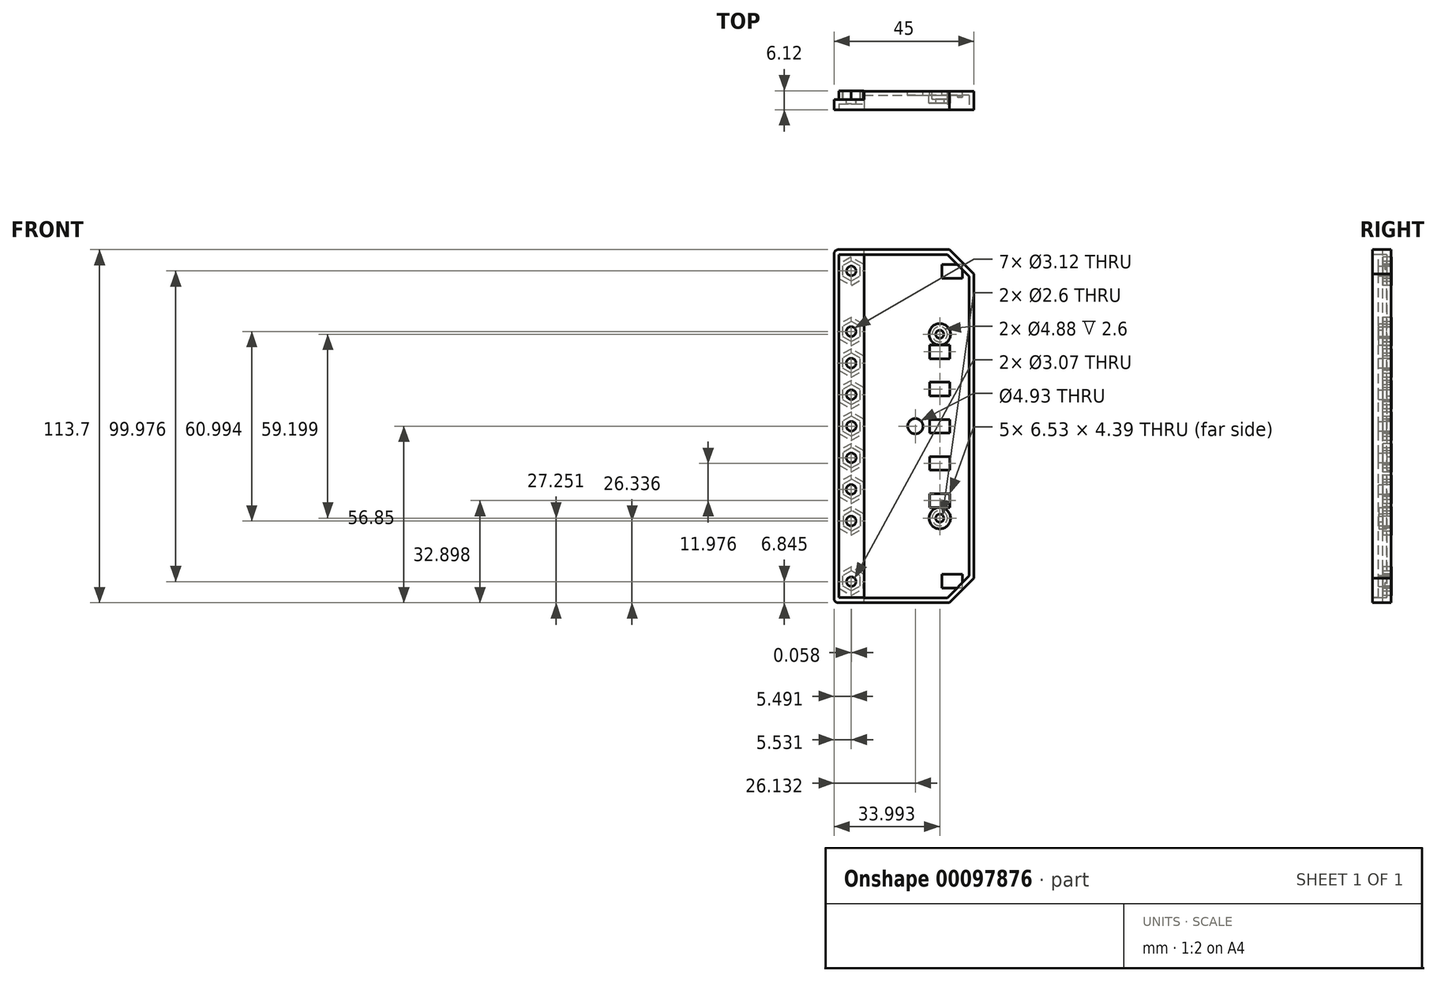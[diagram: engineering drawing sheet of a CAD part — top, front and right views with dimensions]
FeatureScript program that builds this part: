
annotation { "Feature Type Name" : "Feature", "Feature Type Description" : "" }
export const myFeature = defineFeature(function(context is Context, id is Id, definition is map)
    precondition{}
    {
        {
            var Q0;
            Q0=qCreatedBy(makeId("Top.planeOp"),FACE);
            var sketch = newSketch(context, id + "F0", { "sketchPlane" : qUnion([Q0])});
            skLineSegment(sketch, "E0.rect.bottom", {"start": v(22.5, -3) * mm, "end": v(-22.5, -3) * mm});
            skLineSegment(sketch, "E0.rect.top", {"start": v(22.5, 3) * mm, "end": v(-22.5, 3) * mm});
            skLineSegment(sketch, "E0.rect.left", {"start": v(22.5, -3) * mm, "end": v(22.5, 3) * mm});
            skLineSegment(sketch, "E0.rect.right", {"start": v(-22.5, -3) * mm, "end": v(-22.5, 3) * mm});
            skPoint(sketch, "E0.rect.middle", {"position": v(0, 0) * mm});
            skLineSegment(sketch, "E1", {"start": v(-12.85, 3) * mm, "end": v(-12.85, 0.3) * mm});
            skLineSegment(sketch, "E2", {"start": v(-12.85, 0.3) * mm, "end": v(-22.5, 0.3) * mm});
            skSolve(sketch);
        }
        {
            var Q0;
            Q0=qSketchRegion(id+"F0",true);
            extrude(context, id + "F1", {"entities" : qUnion([Q0]), "oppositeDirection" : true, "depth" : 113.7 * mm});
        }
        {
            var Q0;
            {var subQ1=sQuery(id+"F0.wireOp",EDGE,"E1");Q0=makeQuery(id+"F0.imprint","IMPRINT",FACE,{"disambiguationData":[TD([[makeQuery(id+"F0.imprint","IMPRINT",EDGE,{"derivedFrom":subQ1}),-1.0]])]});}
            extrude(context, id + "F2", {"entities" : qUnion([Q0]), "operationType" : NewBodyOperationType.REMOVE, "oppositeDirection" : true, "depth" : 113.93 * mm});
        }
        {
            var Q0;
            Q0=makeQuery(id+"F1.opExtrude","SWEPT_FACE",FACE,{"disambiguationData":[OSD([sQuery(id+"F0.wireOp",EDGE,"E0.rect.bottom")])]});
            var sketch = newSketch(context, id + "F3", { "sketchPlane" : qUnion([Q0])});
            skLineSegment(sketch, "E3.bottom", {"start": v(-22.5, -113.59) * mm, "end": v(-12.85, -113.59) * mm});
            skLineSegment(sketch, "E3.top", {"start": v(-22.5, 0) * mm, "end": v(-12.85, 0) * mm});
            skLineSegment(sketch, "E3.left", {"start": v(-22.5, -113.59) * mm, "end": v(-22.5, 0) * mm});
            skLineSegment(sketch, "E3.right", {"start": v(-12.85, -113.59) * mm, "end": v(-12.85, 0) * mm});
            skLineSegment(sketch, "E4.bottom", {"start": v(-20.92, -112) * mm, "end": v(-12.85, -112) * mm});
            skLineSegment(sketch, "E4.top", {"start": v(-20.92, -1.58) * mm, "end": v(-12.85, -1.58) * mm});
            skLineSegment(sketch, "E4.left", {"start": v(-20.92, -112) * mm, "end": v(-20.92, -1.58) * mm});
            skLineSegment(sketch, "E4.right", {"start": v(-12.85, -112) * mm, "end": v(-12.85, -1.58) * mm});
            skSolve(sketch);
        }
        {
            var Q0;
            Q0=makeQuery(id+"F3.imprint","IMPRINT",FACE,{"disambiguationData":[TD([[makeQuery(id+"F3.imprint","IMPRINT",EDGE,{"derivedFrom":sQuery(id+"F3.wireOp",EDGE,"E4.bottom")}),1.0]])]});
            extrude(context, id + "F4", {"entities" : qUnion([Q0]), "operationType" : NewBodyOperationType.REMOVE, "oppositeDirection" : true, "depth" : 1.9 * mm});
        }
        {
            var Q0;
            Q0=makeQuery(id+"F1.opExtrude","CAP_EDGE",EDGE,{"disambiguationData":[OSD([sQuery(id+"F0.wireOp",EDGE,"E0.rect.left")])],"isStart":false});
            chamfer(context, id + "F5", {"entities" : qUnion([Q0]), "width" : 7.87 * mm, "tangentPropagation" : true});
        }
        {
            var Q0;
            Q0=makeQuery(id+"F1.opExtrude","CAP_EDGE",EDGE,{"disambiguationData":[OSD([sQuery(id+"F0.wireOp",EDGE,"E0.rect.left")])],"isStart":true});
            chamfer(context, id + "F6", {"entities" : qUnion([Q0]), "width" : 7.87 * mm, "tangentPropagation" : true});
        }
        {
            var Q0;
            Q0=makeQuery(id+"F1.opExtrude","SWEPT_FACE",FACE,{"disambiguationData":[OSD([sQuery(id+"F0.wireOp",EDGE,"E0.rect.bottom")])]});
            var sketch = newSketch(context, id + "F7", { "sketchPlane" : qUnion([Q0])});
            skLineSegment(sketch, "E5.bottom", {"start": v(-12.85, -1.58) * mm, "end": v(21, -1.58) * mm});
            skLineSegment(sketch, "E5.top", {"start": v(-12.85, -112.15) * mm, "end": v(21, -112.15) * mm});
            skLineSegment(sketch, "E5.left", {"start": v(-12.85, -1.58) * mm, "end": v(-12.85, -112.15) * mm});
            skLineSegment(sketch, "E5.right", {"start": v(21, -1.58) * mm, "end": v(21, -112.15) * mm});
            skLineSegment(sketch, "E6", {"start": v(21, -105.06) * mm, "end": v(13.92, -112.15) * mm});
            skLineSegment(sketch, "E7", {"start": v(14, -1.58) * mm, "end": v(21, -8.58) * mm});
            skSolve(sketch);
        }
        {
            var Q0;
            {var subQ3=sQuery(id+"F7.wireOp",EDGE,"E5.left");Q0=makeQuery(id+"F7.imprint","IMPRINT",FACE,{"disambiguationData":[TD([[makeQuery(id+"F7.imprint","IMPRINT",EDGE,{"derivedFrom":subQ3}),-1.0]])]});}
            extrude(context, id + "F8", {"entities" : qUnion([Q0]), "operationType" : NewBodyOperationType.REMOVE, "oppositeDirection" : true, "depth" : 4.67 * mm});
        }
        {
            var Q0;
            Q0=makeQuery(id+"F1.opExtrude","SWEPT_FACE",FACE,{"disambiguationData":[OSD([sQuery(id+"F0.wireOp",EDGE,"E0.rect.top")])]});
            var sketch = newSketch(context, id + "F9", { "sketchPlane" : qUnion([Q0])});
            skLineSegment(sketch, "E8", {"start": v(12.85, -56.85) * mm, "end": v(-22.5, -56.85) * mm, "construction": true});
            skLineSegment(sketch, "E9.rect.bottom", {"start": v(-14.76, -59.05) * mm, "end": v(-8.23, -59.05) * mm});
            skLineSegment(sketch, "E9.rect.top", {"start": v(-14.76, -54.65) * mm, "end": v(-8.23, -54.65) * mm});
            skLineSegment(sketch, "E9.rect.left", {"start": v(-14.76, -59.05) * mm, "end": v(-14.76, -54.65) * mm});
            skLineSegment(sketch, "E9.rect.right", {"start": v(-8.23, -59.05) * mm, "end": v(-8.23, -54.65) * mm});
            skPoint(sketch, "E9.rect.middle", {"position": v(-11.5, -56.85) * mm});
            skCircle(sketch, "E10", {"center": v(-3.63, -56.85) * mm, "radius": 2.46 * mm});
            skLineSegment(sketch, "E11.0.1.0", {"start": v(-8.23, -47.07) * mm, "end": v(-8.23, -42.68) * mm});
            skLineSegment(sketch, "E11.0.1.1", {"start": v(-14.76, -47.07) * mm, "end": v(-8.23, -47.07) * mm});
            skLineSegment(sketch, "E11.0.1.2", {"start": v(-14.76, -47.07) * mm, "end": v(-14.76, -42.68) * mm});
            skLineSegment(sketch, "E11.0.1.3", {"start": v(-14.76, -42.68) * mm, "end": v(-8.23, -42.68) * mm});
            skLineSegment(sketch, "E11.0.2.0", {"start": v(-8.23, -35.1) * mm, "end": v(-8.23, -30.7) * mm});
            skLineSegment(sketch, "E11.0.2.1", {"start": v(-14.76, -35.1) * mm, "end": v(-8.23, -35.1) * mm});
            skLineSegment(sketch, "E11.0.2.2", {"start": v(-14.76, -35.1) * mm, "end": v(-14.76, -30.7) * mm});
            skLineSegment(sketch, "E11.0.2.3", {"start": v(-14.76, -30.7) * mm, "end": v(-8.23, -30.7) * mm});
            skLineSegment(sketch, "E11.direction1", {"start": v(-8.23, -59.05) * mm, "end": v(17.17, -59.05) * mm, "construction": true});
            skLineSegment(sketch, "E11.direction2", {"start": v(-8.23, -59.05) * mm, "end": v(-8.23, -47.07) * mm, "construction": true});
            skLineSegment(sketch, "E12.0.1.0", {"start": v(-8.23, -71.02) * mm, "end": v(-8.23, -66.63) * mm});
            skLineSegment(sketch, "E12.0.1.1", {"start": v(-14.76, -71.02) * mm, "end": v(-8.23, -71.02) * mm});
            skLineSegment(sketch, "E12.0.1.2", {"start": v(-14.76, -71.02) * mm, "end": v(-14.76, -66.63) * mm});
            skLineSegment(sketch, "E12.0.1.3", {"start": v(-14.76, -66.63) * mm, "end": v(-8.23, -66.63) * mm});
            skLineSegment(sketch, "E12.0.2.0", {"start": v(-8.23, -83) * mm, "end": v(-8.23, -78.6) * mm});
            skLineSegment(sketch, "E12.0.2.1", {"start": v(-14.76, -83) * mm, "end": v(-8.23, -83) * mm});
            skLineSegment(sketch, "E12.0.2.2", {"start": v(-14.76, -83) * mm, "end": v(-14.76, -78.6) * mm});
            skLineSegment(sketch, "E12.0.2.3", {"start": v(-14.76, -78.6) * mm, "end": v(-8.23, -78.6) * mm});
            skLineSegment(sketch, "E12.direction2", {"start": v(-8.23, -59.05) * mm, "end": v(-8.23, -71.02) * mm, "construction": true});
            skLineSegment(sketch, "E13.rect.bottom", {"start": v(-18.73, -9.2) * mm, "end": v(-12.2, -9.2) * mm});
            skLineSegment(sketch, "E13.rect.top", {"start": v(-18.73, -4.8) * mm, "end": v(-12.2, -4.8) * mm});
            skLineSegment(sketch, "E13.rect.left", {"start": v(-18.73, -9.2) * mm, "end": v(-18.73, -4.8) * mm});
            skLineSegment(sketch, "E13.rect.right", {"start": v(-12.2, -9.2) * mm, "end": v(-12.2, -4.8) * mm});
            skPoint(sketch, "E13.rect.middle", {"position": v(-15.47, -7) * mm});
            skLineSegment(sketch, "E14.rect.bottom", {"start": v(-18.73, -108.9) * mm, "end": v(-12.2, -108.9) * mm});
            skLineSegment(sketch, "E14.rect.top", {"start": v(-18.73, -104.5) * mm, "end": v(-12.2, -104.5) * mm});
            skLineSegment(sketch, "E14.rect.left", {"start": v(-18.73, -108.9) * mm, "end": v(-18.73, -104.5) * mm});
            skLineSegment(sketch, "E14.rect.right", {"start": v(-12.2, -108.9) * mm, "end": v(-12.2, -104.5) * mm});
            skPoint(sketch, "E14.rect.middle", {"position": v(-15.47, -106.7) * mm});
            skSolve(sketch);
        }
        {
            var Q0;
            Q0=qSketchRegion(id+"F9",true);
            extrude(context, id + "F10", {"entities" : qUnion([Q0]), "operationType" : NewBodyOperationType.REMOVE, "oppositeDirection" : true, "depth" : 2 * mm});
        }
        {
            var Q0;
            Q0=makeQuery(id+"F8.boolean.opBoolean","COPY",FACE,{"derivedFrom":makeQuery(id+"F8.opExtrude","CAP_FACE",FACE,{"disambiguationData":[OSD([sQuery(id+"F7.wireOp",EDGE,"E5.bottom"),sQuery(id+"F7.wireOp",EDGE,"E5.top"),sQuery(id+"F7.wireOp",EDGE,"E5.left"),sQuery(id+"F7.wireOp",EDGE,"E5.right"),sQuery(id+"F7.wireOp",EDGE,"E6"),sQuery(id+"F7.wireOp",EDGE,"E7")])],"isStart":false})});
            var sketch = newSketch(context, id + "F11", { "sketchPlane" : qUnion([Q0])});
            skCircle(sketch, "E15", {"center": v(11.5, -27.25) * mm, "radius": 3.45 * mm});
            skCircle(sketch, "E16", {"center": v(11.5, -86.45) * mm, "radius": 3.45 * mm});
            skPoint(sketch, "E17", {"position": v(11.5, -30.7) * mm});
            skPoint(sketch, "E18", {"position": v(11.5, -83) * mm});
            skSolve(sketch);
        }
        {
            var Q0;
            Q0=qSketchRegion(id+"F11",true);
            extrude(context, id + "F12", {"entities" : qUnion([Q0]), "operationType" : NewBodyOperationType.ADD, "depth" : 2.6 * mm});
        }
        {
            var Q0;
            Q0=makeQuery(id+"F12.opExtrude","CAP_FACE",FACE,{"disambiguationData":[OSD([sQuery(id+"F11.wireOp",EDGE,"E16")])],"isStart":false});
            var sketch = newSketch(context, id + "F13", { "sketchPlane" : qUnion([Q0])});
            skCircle(sketch, "E19", {"center": v(11.5, -86.45) * mm, "radius": 1.3 * mm});
            skCircle(sketch, "E20", {"center": v(11.5, -27.25) * mm, "radius": 1.3 * mm});
            skSolve(sketch);
        }
        {
            var Q0;
            Q0=qSketchRegion(id+"F13",true);
            extrude(context, id + "F14", {"entities" : qUnion([Q0]), "operationType" : NewBodyOperationType.REMOVE, "oppositeDirection" : true, "depth" : 25 * mm});
        }
        {
            var Q0;
            Q0=makeQuery(id+"F1.opExtrude","SWEPT_FACE",FACE,{"disambiguationData":[OSD([sQuery(id+"F0.wireOp",EDGE,"E0.rect.top")])]});
            var sketch = newSketch(context, id + "F15", { "sketchPlane" : qUnion([Q0])});
            skCircle(sketch, "E21", {"center": v(-11.5, -27.25) * mm, "radius": 2.44 * mm});
            skCircle(sketch, "E22", {"center": v(-11.5, -86.45) * mm, "radius": 2.44 * mm});
            skSolve(sketch);
        }
        {
            var Q0;
            Q0=qSketchRegion(id+"F15",true);
            extrude(context, id + "F16", {"entities" : qUnion([Q0]), "operationType" : NewBodyOperationType.REMOVE, "oppositeDirection" : true, "depth" : 2.6 * mm});
        }
        {
            var Q0;
            Q0=makeQuery(id+"F1.opExtrude","CAP_EDGE",EDGE,{"disambiguationData":[OSD([sQuery(id+"F0.wireOp",EDGE,"E0.rect.right")])],"isStart":true});
            var Q1;
            Q1=makeQuery(id+"F1.opExtrude","CAP_EDGE",EDGE,{"disambiguationData":[OSD([sQuery(id+"F0.wireOp",EDGE,"E0.rect.right")])],"isStart":false});
            fillet(context, id + "F17", {"entities" : qUnion([Q0, Q1]), "radius" : 1.4 * mm, "tangentPropagation" : true, "allowEdgeOverflow" : false});
        }
        {
            var Q0;
            Q0=makeQuery(id+"F2.boolean.opBoolean","COPY",FACE,{"derivedFrom":makeQuery(id+"F2.opExtrude","SWEPT_FACE",FACE,{"disambiguationData":[OSD([sQuery(id+"F0.wireOp",EDGE,"E2")])]})});
            var sketch = newSketch(context, id + "F18", { "sketchPlane" : qUnion([Q0])});
            skCircle(sketch, "E23.cCircle", {"center": v(16.97, -56.85) * mm, "radius": 3.96 * mm, "construction": true});
            skLineSegment(sketch, "E23.0", {"start": v(16.95, -52.27) * mm, "end": v(20.92, -54.54) * mm});
            skLineSegment(sketch, "E23.1", {"start": v(20.92, -54.54) * mm, "end": v(20.95, -59.12) * mm});
            skLineSegment(sketch, "E23.2", {"start": v(20.95, -59.12) * mm, "end": v(17, -61.43) * mm});
            skLineSegment(sketch, "E23.3", {"start": v(17, -61.43) * mm, "end": v(13.02, -59.16) * mm});
            skLineSegment(sketch, "E23.4", {"start": v(13.02, -59.16) * mm, "end": v(13, -54.58) * mm});
            skLineSegment(sketch, "E23.5", {"start": v(13, -54.58) * mm, "end": v(16.95, -52.27) * mm});
            skPoint(sketch, "E23.0.midPoint", {"position": v(18.94, -53.4) * mm});
            skLineSegment(sketch, "E24", {"start": v(16.97, 0) * mm, "end": v(16.97, -113.7) * mm});
            skLineSegment(sketch, "E25.0.1.0", {"start": v(13, -44.42) * mm, "end": v(16.95, -42.11) * mm});
            skLineSegment(sketch, "E25.0.1.1", {"start": v(13.02, -49) * mm, "end": v(13, -44.42) * mm});
            skLineSegment(sketch, "E25.0.1.2", {"start": v(17, -51.27) * mm, "end": v(13.02, -49) * mm});
            skLineSegment(sketch, "E25.0.1.3", {"start": v(20.95, -48.96) * mm, "end": v(17, -51.27) * mm});
            skLineSegment(sketch, "E25.0.1.4", {"start": v(20.92, -44.38) * mm, "end": v(20.95, -48.96) * mm});
            skLineSegment(sketch, "E25.0.1.5", {"start": v(16.95, -42.11) * mm, "end": v(20.92, -44.38) * mm});
            skLineSegment(sketch, "E25.0.2.0", {"start": v(13, -34.26) * mm, "end": v(16.95, -31.95) * mm});
            skLineSegment(sketch, "E25.0.2.1", {"start": v(13.02, -38.84) * mm, "end": v(13, -34.26) * mm});
            skLineSegment(sketch, "E25.0.2.2", {"start": v(17, -41.1) * mm, "end": v(13.02, -38.84) * mm});
            skLineSegment(sketch, "E25.0.2.3", {"start": v(20.95, -38.8) * mm, "end": v(17, -41.1) * mm});
            skLineSegment(sketch, "E25.0.2.4", {"start": v(20.92, -34.22) * mm, "end": v(20.95, -38.8) * mm});
            skLineSegment(sketch, "E25.0.2.5", {"start": v(16.95, -31.95) * mm, "end": v(20.92, -34.22) * mm});
            skLineSegment(sketch, "E25.0.3.0", {"start": v(13, -24.1) * mm, "end": v(16.95, -21.8) * mm});
            skLineSegment(sketch, "E25.0.3.1", {"start": v(13.02, -28.68) * mm, "end": v(13, -24.1) * mm});
            skLineSegment(sketch, "E25.0.3.2", {"start": v(17, -30.95) * mm, "end": v(13.02, -28.68) * mm});
            skLineSegment(sketch, "E25.0.3.3", {"start": v(20.95, -28.64) * mm, "end": v(17, -30.95) * mm});
            skLineSegment(sketch, "E25.0.3.4", {"start": v(20.92, -24.06) * mm, "end": v(20.95, -28.64) * mm});
            skLineSegment(sketch, "E25.0.3.5", {"start": v(16.95, -21.8) * mm, "end": v(20.92, -24.06) * mm});
            skLineSegment(sketch, "E25.direction1", {"start": v(13, -54.58) * mm, "end": v(38.4, -54.58) * mm, "construction": true});
            skLineSegment(sketch, "E25.direction2", {"start": v(13, -54.58) * mm, "end": v(13, -44.42) * mm, "construction": true});
            skLineSegment(sketch, "E26.1.0.0", {"start": v(13.02, -69.32) * mm, "end": v(13, -64.74) * mm});
            skLineSegment(sketch, "E26.1.0.1", {"start": v(17, -71.59) * mm, "end": v(13.02, -69.32) * mm});
            skLineSegment(sketch, "E26.1.0.2", {"start": v(20.94, -69.28) * mm, "end": v(17, -71.59) * mm});
            skLineSegment(sketch, "E26.1.0.3", {"start": v(20.92, -64.7) * mm, "end": v(20.94, -69.28) * mm});
            skLineSegment(sketch, "E26.1.0.4", {"start": v(16.95, -62.43) * mm, "end": v(20.92, -64.7) * mm});
            skLineSegment(sketch, "E26.1.0.5", {"start": v(13, -64.74) * mm, "end": v(16.95, -62.43) * mm});
            skLineSegment(sketch, "E26.2.0.0", {"start": v(13.01, -79.48) * mm, "end": v(12.99, -74.9) * mm});
            skLineSegment(sketch, "E26.2.0.1", {"start": v(16.99, -81.75) * mm, "end": v(13.01, -79.48) * mm});
            skLineSegment(sketch, "E26.2.0.2", {"start": v(20.94, -79.44) * mm, "end": v(16.99, -81.75) * mm});
            skLineSegment(sketch, "E26.2.0.3", {"start": v(20.91, -74.86) * mm, "end": v(20.94, -79.44) * mm});
            skLineSegment(sketch, "E26.2.0.4", {"start": v(16.94, -72.6) * mm, "end": v(20.91, -74.86) * mm});
            skLineSegment(sketch, "E26.2.0.5", {"start": v(12.99, -74.9) * mm, "end": v(16.94, -72.6) * mm});
            skLineSegment(sketch, "E26.3.0.0", {"start": v(13, -89.64) * mm, "end": v(12.99, -85.06) * mm});
            skLineSegment(sketch, "E26.3.0.1", {"start": v(16.98, -91.9) * mm, "end": v(13, -89.64) * mm});
            skLineSegment(sketch, "E26.3.0.2", {"start": v(20.93, -89.6) * mm, "end": v(16.98, -91.9) * mm});
            skLineSegment(sketch, "E26.3.0.3", {"start": v(20.9, -85.02) * mm, "end": v(20.93, -89.6) * mm});
            skLineSegment(sketch, "E26.3.0.4", {"start": v(16.94, -82.75) * mm, "end": v(20.9, -85.02) * mm});
            skLineSegment(sketch, "E26.3.0.5", {"start": v(12.99, -85.06) * mm, "end": v(16.94, -82.75) * mm});
            skLineSegment(sketch, "E26.direction1", {"start": v(13.02, -59.16) * mm, "end": v(13.02, -69.32) * mm, "construction": true});
            skCircle(sketch, "E27.cCircle", {"center": v(16.97, -7.02) * mm, "radius": 3.96 * mm, "construction": true});
            skLineSegment(sketch, "E27.0", {"start": v(16.93, -11.6) * mm, "end": v(13, -9.27) * mm});
            skLineSegment(sketch, "E27.1", {"start": v(13, -9.27) * mm, "end": v(13.03, -4.7) * mm});
            skLineSegment(sketch, "E27.2", {"start": v(13.03, -4.7) * mm, "end": v(17.02, -2.44) * mm});
            skLineSegment(sketch, "E27.3", {"start": v(17.02, -2.44) * mm, "end": v(20.96, -4.77) * mm});
            skLineSegment(sketch, "E27.4", {"start": v(20.96, -4.77) * mm, "end": v(20.91, -9.34) * mm});
            skLineSegment(sketch, "E27.5", {"start": v(20.91, -9.34) * mm, "end": v(16.93, -11.6) * mm});
            skPoint(sketch, "E27.0.midPoint", {"position": v(14.96, -10.43) * mm});
            skCircle(sketch, "E28.cCircle", {"center": v(16.97, -106.72) * mm, "radius": 3.96 * mm, "construction": true});
            skLineSegment(sketch, "E28.0", {"start": v(13, -104.47) * mm, "end": v(16.93, -102.15) * mm});
            skLineSegment(sketch, "E28.1", {"start": v(16.93, -102.15) * mm, "end": v(20.91, -104.4) * mm});
            skLineSegment(sketch, "E28.2", {"start": v(20.91, -104.4) * mm, "end": v(20.96, -108.97) * mm});
            skLineSegment(sketch, "E28.3", {"start": v(20.96, -108.97) * mm, "end": v(17.02, -111.3) * mm});
            skLineSegment(sketch, "E28.4", {"start": v(17.02, -111.3) * mm, "end": v(13.03, -109.05) * mm});
            skLineSegment(sketch, "E28.5", {"start": v(13.03, -109.05) * mm, "end": v(13, -104.47) * mm});
            skPoint(sketch, "E28.0.midPoint", {"position": v(14.96, -103.3) * mm});
            skSolve(sketch);
        }
        {
            var Q0;
            Q0=qSketchRegion(id+"F18",true);
            extrude(context, id + "F19", {"entities" : qUnion([Q0]), "operationType" : NewBodyOperationType.ADD, "depth" : 2.82 * mm});
        }
        {
            var Q0;
            Q0=makeQuery(id+"F19.opExtrude","CAP_FACE",FACE,{"disambiguationData":[OSD([sQuery(id+"F18.wireOp",EDGE,"E23.0"),sQuery(id+"F18.wireOp",EDGE,"E23.1"),sQuery(id+"F18.wireOp",EDGE,"E23.2"),sQuery(id+"F18.wireOp",EDGE,"E23.3"),sQuery(id+"F18.wireOp",EDGE,"E23.4"),sQuery(id+"F18.wireOp",EDGE,"E23.5")])],"isStart":false});
            var sketch = newSketch(context, id + "F20", { "sketchPlane" : qUnion([Q0])});
            skCircle(sketch, "E29.cCircle", {"center": v(16.95, -56.85) * mm, "radius": 2.82 * mm, "construction": true});
            skLineSegment(sketch, "E29.0", {"start": v(16.93, -53.6) * mm, "end": v(19.76, -55.2) * mm});
            skLineSegment(sketch, "E29.1", {"start": v(19.76, -55.2) * mm, "end": v(19.78, -58.46) * mm});
            skLineSegment(sketch, "E29.2", {"start": v(19.78, -58.46) * mm, "end": v(16.97, -60.1) * mm});
            skLineSegment(sketch, "E29.3", {"start": v(16.97, -60.1) * mm, "end": v(14.14, -58.5) * mm});
            skLineSegment(sketch, "E29.4", {"start": v(14.14, -58.5) * mm, "end": v(14.12, -55.24) * mm});
            skLineSegment(sketch, "E29.5", {"start": v(14.12, -55.24) * mm, "end": v(16.93, -53.6) * mm});
            skPoint(sketch, "E29.0.midPoint", {"position": v(18.35, -54.4) * mm});
            skLineSegment(sketch, "E30", {"start": v(16.95, 0) * mm, "end": v(16.95, -113.7) * mm, "construction": true});
            skLineSegment(sketch, "E31.0.1.0", {"start": v(19.76, -45.05) * mm, "end": v(19.78, -48.3) * mm});
            skLineSegment(sketch, "E31.0.1.1", {"start": v(16.93, -43.43) * mm, "end": v(19.76, -45.05) * mm});
            skLineSegment(sketch, "E31.0.1.2", {"start": v(14.12, -45.08) * mm, "end": v(16.93, -43.43) * mm});
            skLineSegment(sketch, "E31.0.1.3", {"start": v(14.14, -48.33) * mm, "end": v(14.12, -45.08) * mm});
            skLineSegment(sketch, "E31.0.1.4", {"start": v(16.97, -49.95) * mm, "end": v(14.14, -48.33) * mm});
            skLineSegment(sketch, "E31.0.1.5", {"start": v(19.78, -48.3) * mm, "end": v(16.97, -49.95) * mm});
            skLineSegment(sketch, "E31.0.2.0", {"start": v(19.76, -34.89) * mm, "end": v(19.78, -38.14) * mm});
            skLineSegment(sketch, "E31.0.2.1", {"start": v(16.93, -33.27) * mm, "end": v(19.76, -34.89) * mm});
            skLineSegment(sketch, "E31.0.2.2", {"start": v(14.12, -34.92) * mm, "end": v(16.93, -33.27) * mm});
            skLineSegment(sketch, "E31.0.2.3", {"start": v(14.14, -38.17) * mm, "end": v(14.12, -34.92) * mm});
            skLineSegment(sketch, "E31.0.2.4", {"start": v(16.97, -39.79) * mm, "end": v(14.14, -38.17) * mm});
            skLineSegment(sketch, "E31.0.2.5", {"start": v(19.78, -38.14) * mm, "end": v(16.97, -39.79) * mm});
            skLineSegment(sketch, "E31.0.3.0", {"start": v(19.76, -24.73) * mm, "end": v(19.78, -27.98) * mm});
            skLineSegment(sketch, "E31.0.3.1", {"start": v(16.93, -23.11) * mm, "end": v(19.76, -24.73) * mm});
            skLineSegment(sketch, "E31.0.3.2", {"start": v(14.12, -24.76) * mm, "end": v(16.93, -23.11) * mm});
            skLineSegment(sketch, "E31.0.3.3", {"start": v(14.14, -28.01) * mm, "end": v(14.12, -24.76) * mm});
            skLineSegment(sketch, "E31.0.3.4", {"start": v(16.97, -29.63) * mm, "end": v(14.14, -28.01) * mm});
            skLineSegment(sketch, "E31.0.3.5", {"start": v(19.78, -27.98) * mm, "end": v(16.97, -29.63) * mm});
            skLineSegment(sketch, "E31.direction1", {"start": v(19.78, -58.46) * mm, "end": v(45.18, -58.46) * mm, "construction": true});
            skLineSegment(sketch, "E31.direction2", {"start": v(19.78, -58.46) * mm, "end": v(19.78, -48.3) * mm, "construction": true});
            skLineSegment(sketch, "E32.1.0.0", {"start": v(14.08, -68.65) * mm, "end": v(14.06, -65.4) * mm});
            skLineSegment(sketch, "E32.1.0.1", {"start": v(14.06, -65.4) * mm, "end": v(16.87, -63.75) * mm});
            skPoint(sketch, "E32.1.0.2", {"position": v(18.29, -64.56) * mm});
            skLineSegment(sketch, "E32.1.0.3", {"start": v(19.7, -65.37) * mm, "end": v(19.72, -68.62) * mm});
            skLineSegment(sketch, "E32.1.0.4", {"start": v(16.87, -63.75) * mm, "end": v(19.7, -65.37) * mm});
            skLineSegment(sketch, "E32.1.0.5", {"start": v(19.72, -68.62) * mm, "end": v(16.91, -70.27) * mm});
            skLineSegment(sketch, "E32.1.0.6", {"start": v(16.91, -70.27) * mm, "end": v(14.08, -68.65) * mm});
            skLineSegment(sketch, "E32.2.0.0", {"start": v(14.03, -78.81) * mm, "end": v(14, -75.56) * mm});
            skLineSegment(sketch, "E32.2.0.1", {"start": v(14, -75.56) * mm, "end": v(16.82, -73.91) * mm});
            skPoint(sketch, "E32.2.0.2", {"position": v(18.23, -74.72) * mm});
            skLineSegment(sketch, "E32.2.0.3", {"start": v(19.65, -75.53) * mm, "end": v(19.67, -78.78) * mm});
            skLineSegment(sketch, "E32.2.0.4", {"start": v(16.82, -73.91) * mm, "end": v(19.65, -75.53) * mm});
            skLineSegment(sketch, "E32.2.0.5", {"start": v(19.67, -78.78) * mm, "end": v(16.86, -80.43) * mm});
            skLineSegment(sketch, "E32.2.0.6", {"start": v(16.86, -80.43) * mm, "end": v(14.03, -78.81) * mm});
            skLineSegment(sketch, "E32.3.0.0", {"start": v(13.97, -88.97) * mm, "end": v(13.95, -85.72) * mm});
            skLineSegment(sketch, "E32.3.0.1", {"start": v(13.95, -85.72) * mm, "end": v(16.76, -84.07) * mm});
            skPoint(sketch, "E32.3.0.2", {"position": v(18.17, -84.88) * mm});
            skLineSegment(sketch, "E32.3.0.3", {"start": v(19.59, -85.68) * mm, "end": v(19.6, -88.94) * mm});
            skLineSegment(sketch, "E32.3.0.4", {"start": v(16.76, -84.07) * mm, "end": v(19.59, -85.68) * mm});
            skLineSegment(sketch, "E32.3.0.5", {"start": v(19.6, -88.94) * mm, "end": v(16.8, -90.59) * mm});
            skLineSegment(sketch, "E32.3.0.6", {"start": v(16.8, -90.59) * mm, "end": v(13.97, -88.97) * mm});
            skLineSegment(sketch, "E32.direction1", {"start": v(14.14, -58.5) * mm, "end": v(14.08, -68.65) * mm, "construction": true});
            skCircle(sketch, "E33.cCircle", {"center": v(16.95, -106.62) * mm, "radius": 2.82 * mm, "construction": true});
            skLineSegment(sketch, "E33.0", {"start": v(14.12, -105) * mm, "end": v(16.94, -103.36) * mm});
            skLineSegment(sketch, "E33.1", {"start": v(16.94, -103.36) * mm, "end": v(19.76, -104.98) * mm});
            skLineSegment(sketch, "E33.2", {"start": v(19.76, -104.98) * mm, "end": v(19.78, -108.24) * mm});
            skLineSegment(sketch, "E33.3", {"start": v(19.78, -108.24) * mm, "end": v(16.96, -109.88) * mm});
            skLineSegment(sketch, "E33.4", {"start": v(16.96, -109.88) * mm, "end": v(14.14, -108.26) * mm});
            skLineSegment(sketch, "E33.5", {"start": v(14.14, -108.26) * mm, "end": v(14.12, -105) * mm});
            skPoint(sketch, "E33.0.midPoint", {"position": v(15.53, -104.18) * mm});
            skCircle(sketch, "E34.cCircle", {"center": v(16.95, -6.88) * mm, "radius": 2.82 * mm, "construction": true});
            skPoint(sketch, "E34.cCircle.perimeterSnap0", {"position": v(15.56, -38.98) * mm});
            skLineSegment(sketch, "E34.0", {"start": v(14.12, -5.26) * mm, "end": v(16.93, -3.62) * mm});
            skLineSegment(sketch, "E34.1", {"start": v(16.93, -3.62) * mm, "end": v(19.76, -5.23) * mm});
            skLineSegment(sketch, "E34.2", {"start": v(19.76, -5.23) * mm, "end": v(19.78, -8.49) * mm});
            skLineSegment(sketch, "E34.3", {"start": v(19.78, -8.49) * mm, "end": v(16.97, -10.13) * mm});
            skLineSegment(sketch, "E34.4", {"start": v(16.97, -10.13) * mm, "end": v(14.14, -8.52) * mm});
            skLineSegment(sketch, "E34.5", {"start": v(14.14, -8.52) * mm, "end": v(14.12, -5.26) * mm});
            skPoint(sketch, "E34.0.midPoint", {"position": v(15.53, -4.44) * mm});
            skSolve(sketch);
        }
        {
            var Q0;
            Q0=qSketchRegion(id+"F20",true);
            extrude(context, id + "F21", {"entities" : qUnion([Q0]), "operationType" : NewBodyOperationType.REMOVE, "oppositeDirection" : true, "depth" : 2.82 * mm});
        }
        {
            var Q0;
            Q0=makeQuery(id+"F21.boolean.opBoolean","COPY",FACE,{"derivedFrom":makeQuery(id+"F21.opExtrude","CAP_FACE",FACE,{"disambiguationData":[OSD([sQuery(id+"F20.wireOp",EDGE,"E29.0"),sQuery(id+"F20.wireOp",EDGE,"E29.1"),sQuery(id+"F20.wireOp",EDGE,"E29.2"),sQuery(id+"F20.wireOp",EDGE,"E29.3"),sQuery(id+"F20.wireOp",EDGE,"E29.4"),sQuery(id+"F20.wireOp",EDGE,"E29.5")])],"isStart":false})});
            var sketch = newSketch(context, id + "F22", { "sketchPlane" : qUnion([Q0])});
            skLineSegment(sketch, "E35", {"start": v(16.93, -53.6) * mm, "end": v(16.97, -60.1) * mm, "construction": true});
            skCircle(sketch, "E36", {"center": v(16.95, -56.85) * mm, "radius": 1.56 * mm});
            skCircle(sketch, "E37.0.1.0", {"center": v(16.97, -46.7) * mm, "radius": 1.56 * mm});
            skCircle(sketch, "E37.0.2.0", {"center": v(16.99, -36.53) * mm, "radius": 1.56 * mm});
            skCircle(sketch, "E37.0.3.0", {"center": v(17, -26.37) * mm, "radius": 1.56 * mm});
            skLineSegment(sketch, "E37.direction1", {"start": v(16.95, -56.85) * mm, "end": v(42.35, -56.85) * mm, "construction": true});
            skLineSegment(sketch, "E37.direction2", {"start": v(16.95, -56.85) * mm, "end": v(16.97, -46.7) * mm, "construction": true});
            skCircle(sketch, "E38", {"center": v(16.97, -6.88) * mm, "radius": 1.54 * mm});
            skLineSegment(sketch, "E39", {"start": v(16.97, -10.13) * mm, "end": v(16.97, -3.63) * mm, "construction": true});
            skLineSegment(sketch, "E40", {"start": v(14.13, -56.87) * mm, "end": v(19.77, -56.87) * mm, "construction": true});
            skCircle(sketch, "E41.MirrorC", {"center": v(16.97, -67.04) * mm, "radius": 1.56 * mm});
            skCircle(sketch, "E42.MirrorC", {"center": v(16.99, -77.2) * mm, "radius": 1.56 * mm});
            skCircle(sketch, "E43.MirrorC", {"center": v(17, -87.36) * mm, "radius": 1.56 * mm});
            skCircle(sketch, "E44.MirrorC", {"center": v(16.97, -106.86) * mm, "radius": 1.54 * mm});
            skSolve(sketch);
        }
        {
            var Q0;
            Q0=qSketchRegion(id+"F22",true);
            extrude(context, id + "F23", {"entities" : qUnion([Q0]), "operationType" : NewBodyOperationType.REMOVE, "oppositeDirection" : true, "depth" : 25.4 * mm});
        }
    });
